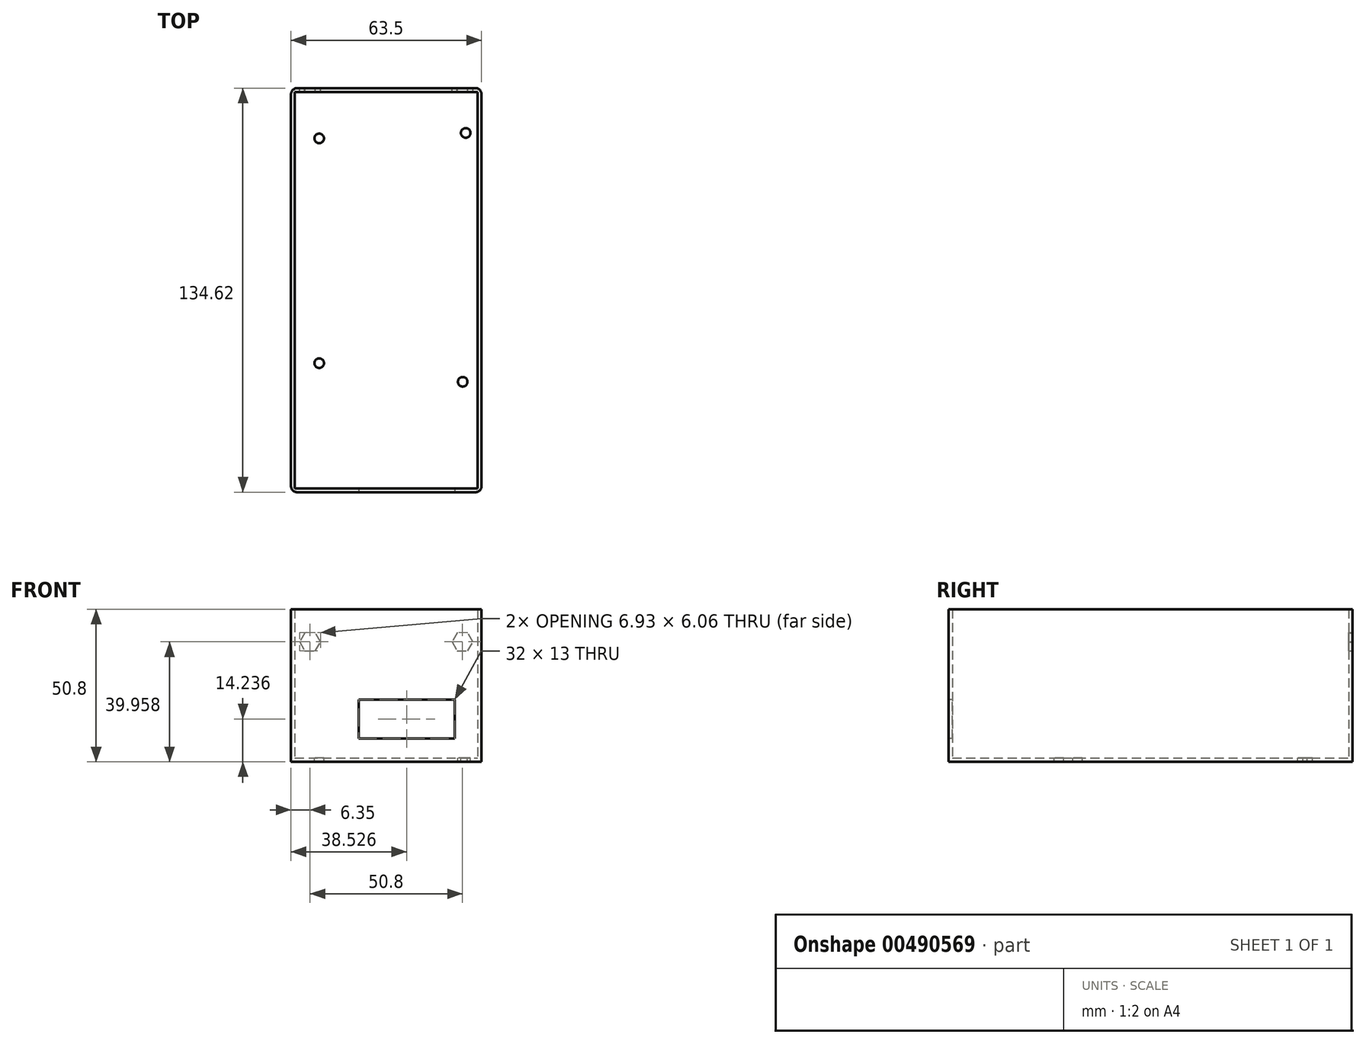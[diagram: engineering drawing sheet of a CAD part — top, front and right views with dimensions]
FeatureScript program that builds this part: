
annotation { "Feature Type Name" : "Feature", "Feature Type Description" : "" }
export const myFeature = defineFeature(function(context is Context, id is Id, definition is map)
    precondition{}
    {
        {
            var Q0;
            Q0=qCreatedBy(makeId("Front.planeOp"),FACE);
            var sketch = newSketch(context, id + "F0", { "sketchPlane" : qUnion([Q0])});
            skLineSegment(sketch, "E0.bottom", {"start": v(-31.75, 25.4) * mm, "end": v(31.75, 25.4) * mm});
            skLineSegment(sketch, "E0.top", {"start": v(-31.75, -25.4) * mm, "end": v(31.75, -25.4) * mm});
            skLineSegment(sketch, "E0.left", {"start": v(-31.75, 25.4) * mm, "end": v(-31.75, -25.4) * mm});
            skLineSegment(sketch, "E0.right", {"start": v(31.75, 25.4) * mm, "end": v(31.75, -25.4) * mm});
            skPoint(sketch, "E0.middle", {"position": v(0, 0) * mm});
            skSolve(sketch);
        }
        {
            var Q0;
            Q0=makeQuery(id+"F0.imprint","IMPRINT",FACE,{"disambiguationData":[TD([[makeQuery(id+"F0.imprint","IMPRINT",EDGE,{"derivedFrom":sQuery(id+"F0.wireOp",EDGE,"E0.bottom")}),-1.0]])]});
            extrude(context, id + "F1", {"entities" : qUnion([Q0]), "depth" : 134.62 * mm});
        }
        {
            var Q0;
            Q0=makeQuery(id+"F1.opExtrude","SWEPT_FACE",FACE,{"disambiguationData":[OSD([sQuery(id+"F0.wireOp",EDGE,"E0.bottom")])]});
            shell(context, id + "F2", {"entities" : qUnion([Q0]), "thickness" : 1.27 * mm});
        }
        {
            var Q0;
            Q0=makeQuery(id+"F1.opExtrude","CAP_FACE",FACE,{"disambiguationData":[OSD([sQuery(id+"F0.wireOp",EDGE,"E0.bottom"),sQuery(id+"F0.wireOp",EDGE,"E0.top"),sQuery(id+"F0.wireOp",EDGE,"E0.left"),sQuery(id+"F0.wireOp",EDGE,"E0.right")])],"isStart":false});
            var sketch = newSketch(context, id + "F3", { "sketchPlane" : qUnion([Q0])});
            skLineSegment(sketch, "E1.bottom", {"start": v(22.78, -17.66) * mm, "end": v(-9.22, -17.66) * mm});
            skLineSegment(sketch, "E1.top", {"start": v(22.78, -4.66) * mm, "end": v(-9.22, -4.66) * mm});
            skLineSegment(sketch, "E1.left", {"start": v(22.78, -17.66) * mm, "end": v(22.78, -4.66) * mm});
            skLineSegment(sketch, "E1.right", {"start": v(-9.22, -17.66) * mm, "end": v(-9.22, -4.66) * mm});
            skPoint(sketch, "E1.middle", {"position": v(6.78, -11.16) * mm});
            skSolve(sketch);
        }
        {
            var Q0;
            Q0=makeQuery(id+"F3.imprint","IMPRINT",FACE,{"disambiguationData":[TD([[makeQuery(id+"F3.imprint","IMPRINT",EDGE,{"derivedFrom":sQuery(id+"F3.wireOp",EDGE,"E1.bottom")}),-1.0]])]});
            extrude(context, id + "F4", {"entities" : qUnion([Q0]), "operationType" : NewBodyOperationType.REMOVE, "oppositeDirection" : true, "depth" : 25.4 * mm});
        }
        {
            var Q0;
            Q0=makeQuery(id+"F1.opExtrude","CAP_FACE",FACE,{"disambiguationData":[OSD([sQuery(id+"F0.wireOp",EDGE,"E0.bottom"),sQuery(id+"F0.wireOp",EDGE,"E0.top"),sQuery(id+"F0.wireOp",EDGE,"E0.left"),sQuery(id+"F0.wireOp",EDGE,"E0.right")])],"isStart":true});
            var sketch = newSketch(context, id + "F5", { "sketchPlane" : qUnion([Q0])});
            skCircle(sketch, "E2.cCircle", {"center": v(-25.4, 14.56) * mm, "radius": 3.46 * mm, "construction": true});
            skLineSegment(sketch, "E2.0", {"start": v(-23.72, 17.59) * mm, "end": v(-21.94, 14.62) * mm});
            skLineSegment(sketch, "E2.1", {"start": v(-21.94, 14.62) * mm, "end": v(-23.62, 11.59) * mm});
            skLineSegment(sketch, "E2.2", {"start": v(-23.62, 11.59) * mm, "end": v(-27.08, 11.53) * mm});
            skLineSegment(sketch, "E2.3", {"start": v(-27.08, 11.53) * mm, "end": v(-28.86, 14.5) * mm});
            skLineSegment(sketch, "E2.4", {"start": v(-28.86, 14.5) * mm, "end": v(-27.18, 17.53) * mm});
            skLineSegment(sketch, "E2.5", {"start": v(-27.18, 17.53) * mm, "end": v(-23.72, 17.59) * mm});
            skCircle(sketch, "E3.1.0.0", {"center": v(25.4, 14.56) * mm, "radius": 3.46 * mm, "construction": true});
            skLineSegment(sketch, "E3.1.0.1", {"start": v(23.72, 11.53) * mm, "end": v(21.94, 14.5) * mm});
            skLineSegment(sketch, "E3.1.0.2", {"start": v(27.18, 11.59) * mm, "end": v(23.72, 11.53) * mm});
            skLineSegment(sketch, "E3.1.0.3", {"start": v(21.94, 14.5) * mm, "end": v(23.62, 17.53) * mm});
            skLineSegment(sketch, "E3.1.0.4", {"start": v(23.62, 17.53) * mm, "end": v(27.08, 17.59) * mm});
            skLineSegment(sketch, "E3.1.0.5", {"start": v(27.08, 17.59) * mm, "end": v(28.86, 14.62) * mm});
            skLineSegment(sketch, "E3.1.0.6", {"start": v(28.86, 14.62) * mm, "end": v(27.18, 11.59) * mm});
            skLineSegment(sketch, "E3.direction1", {"start": v(-25.4, 14.56) * mm, "end": v(25.4, 14.56) * mm, "construction": true});
            skSolve(sketch);
        }
        {
            var Q0;
            Q0=makeQuery(id+"F2.opShell","OFFSET_FACE",FACE,{"disambiguationData":[OSD([sQuery(id+"F0.wireOp",EDGE,"E0.top")])]});
            var sketch = newSketch(context, id + "F6", { "sketchPlane" : qUnion([Q0])});
            skPoint(sketch, "E4", {"position": v(-22.34, -91.63) * mm});
            skPoint(sketch, "E5", {"position": v(25.47, -97.83) * mm});
            skPoint(sketch, "E6", {"position": v(-22.34, -16.73) * mm});
            skPoint(sketch, "E7", {"position": v(26.48, -14.93) * mm});
            skCircle(sketch, "E8", {"center": v(-22.34, -16.73) * mm, "radius": 1.6 * mm});
            skCircle(sketch, "E9", {"center": v(26.48, -14.93) * mm, "radius": 1.6 * mm});
            skCircle(sketch, "E10", {"center": v(-22.34, -91.63) * mm, "radius": 1.6 * mm});
            skCircle(sketch, "E11", {"center": v(25.47, -97.83) * mm, "radius": 1.6 * mm});
            skSolve(sketch);
        }
        {
            var Q0;
            Q0=makeQuery(id+"F6.imprint","IMPRINT",FACE,{"disambiguationData":[TD([[makeQuery(id+"F6.imprint","IMPRINT",EDGE,{"derivedFrom":sQuery(id+"F6.wireOp",EDGE,"E8")}),1.0]])]});
            var Q1;
            {var subQ0=sQuery(id+"F6.wireOp",EDGE,"E9");var subQ1=makeQuery(id+"F2.opShell","OFFSET_EDGE",EDGE,{"disambiguationData":[OSD([sQuery(id+"F0.wireOp",EDGE,"E0.top"),sQuery(id+"F0.wireOp",EDGE,"E0.right")])]});var subQ2=makeQuery(id+"F6.imprint","INTERSECT",VERTEX,{"disambiguationData":[OD(0.0)],"derivedFrom":[subQ1,subQ0]});Q1=makeQuery(id+"F6.imprint","IMPRINT",FACE,{"disambiguationData":[TD([[makeQuery(id+"F6.imprint","IMPRINT",EDGE,{"disambiguationData":[TD([[subQ2,-1.0]])],"derivedFrom":subQ0}),1.0]])]});}
            var Q2;
            Q2=makeQuery(id+"F6.imprint","IMPRINT",FACE,{"disambiguationData":[TD([[makeQuery(id+"F6.imprint","IMPRINT",EDGE,{"derivedFrom":sQuery(id+"F6.wireOp",EDGE,"E10")}),1.0]])]});
            var Q3;
            Q3=makeQuery(id+"F6.imprint","IMPRINT",FACE,{"disambiguationData":[TD([[makeQuery(id+"F6.imprint","IMPRINT",EDGE,{"derivedFrom":sQuery(id+"F6.wireOp",EDGE,"E11")}),1.0]])]});
            extrude(context, id + "F7", {"entities" : qUnion([Q0, Q1, Q2, Q3]), "operationType" : NewBodyOperationType.REMOVE, "oppositeDirection" : true, "depth" : 25.4 * mm});
        }
        {
            var Q0;
            Q0=makeQuery(id+"F1.opExtrude","CAP_EDGE",EDGE,{"disambiguationData":[OSD([sQuery(id+"F0.wireOp",EDGE,"E0.left")])],"isStart":false});
            fillet(context, id + "F8", {"entities" : qUnion([Q0]), "radius" : 2.03 * mm, "tangentPropagation" : true, "allowEdgeOverflow" : false});
        }
        {
            var Q0;
            Q0=makeQuery(id+"F1.opExtrude","CAP_EDGE",EDGE,{"disambiguationData":[OSD([sQuery(id+"F0.wireOp",EDGE,"E0.right")])],"isStart":false});
            fillet(context, id + "F9", {"entities" : qUnion([Q0]), "radius" : 2.03 * mm, "tangentPropagation" : true, "allowEdgeOverflow" : false});
        }
        {
            var Q0;
            Q0=makeQuery(id+"F1.opExtrude","CAP_EDGE",EDGE,{"disambiguationData":[OSD([sQuery(id+"F0.wireOp",EDGE,"E0.right")])],"isStart":true});
            var Q1;
            Q1=makeQuery(id+"F1.opExtrude","CAP_EDGE",EDGE,{"disambiguationData":[OSD([sQuery(id+"F0.wireOp",EDGE,"E0.left")])],"isStart":true});
            fillet(context, id + "F10", {"entities" : qUnion([Q0, Q1]), "radius" : 2.03 * mm, "tangentPropagation" : true, "allowEdgeOverflow" : false});
        }
        {
            var Q0;
            Q0=qSketchRegion(id+"F5",true);
            extrude(context, id + "F11", {"entities" : qUnion([Q0]), "operationType" : NewBodyOperationType.REMOVE, "oppositeDirection" : true, "depth" : 25.4 * mm});
        }
    });
